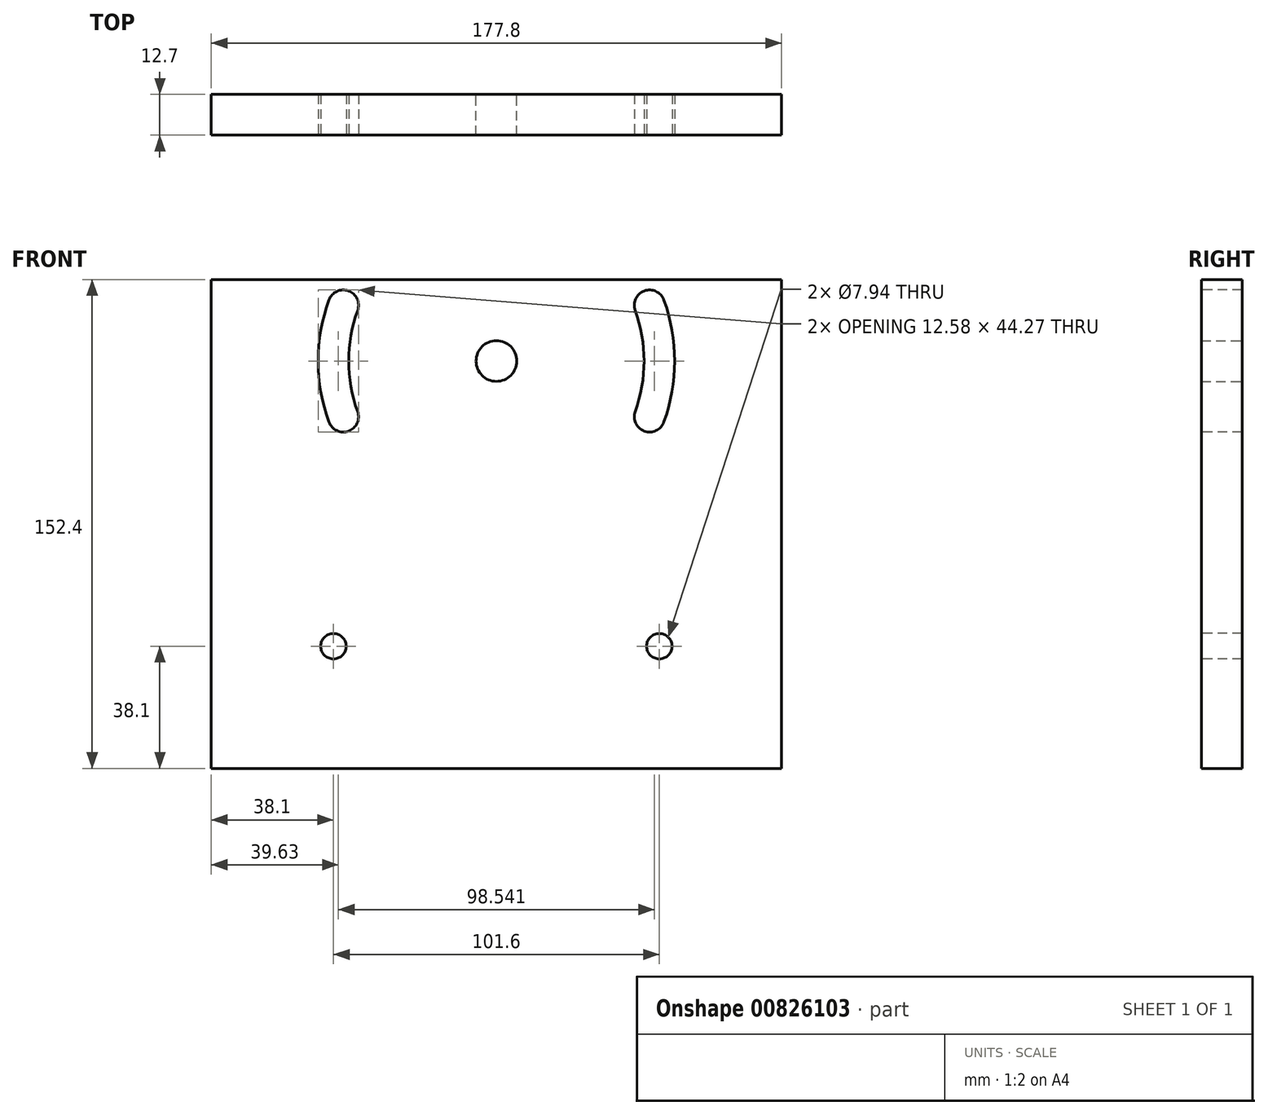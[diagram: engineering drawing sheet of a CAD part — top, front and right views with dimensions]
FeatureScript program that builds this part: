
annotation { "Feature Type Name" : "Feature", "Feature Type Description" : "" }
export const myFeature = defineFeature(function(context is Context, id is Id, definition is map)
    precondition{}
    {
        {
            var Q0;
            Q0=qCreatedBy(makeId("Front.planeOp"),FACE);
            var sketch = newSketch(context, id + "F0", { "sketchPlane" : qUnion([Q0])});
            skCircle(sketch, "E0", {"center": v(0, 0) * mm, "radius": 6.35 * mm});
            skLineSegment(sketch, "E1.bottom", {"start": v(-95.25, -127) * mm, "end": v(88.9, -127) * mm});
            skLineSegment(sketch, "E1.top", {"start": v(-95.25, 25.4) * mm, "end": v(88.9, 25.4) * mm});
            skLineSegment(sketch, "E1.left", {"start": v(-95.25, -127) * mm, "end": v(-95.25, 25.4) * mm});
            skLineSegment(sketch, "E1.right", {"start": v(88.9, -127) * mm, "end": v(88.9, 25.4) * mm});
            skSolve(sketch);
        }
        {
            var Q0;
            Q0=qSketchRegion(id+"F0",true);
            extrude(context, id + "F1", {"entities" : qUnion([Q0]), "depth" : 12.7 * mm, "offsetDistance" : 25.4 * mm});
        }
        {
            var Q0;
            Q0=makeQuery(id+"F1.opExtrude","CAP_FACE",FACE,{"disambiguationData":[OSD([sQuery(id+"F0.wireOp",EDGE,"E0"),sQuery(id+"F0.wireOp",EDGE,"E1.bottom"),sQuery(id+"F0.wireOp",EDGE,"E1.top"),sQuery(id+"F0.wireOp",EDGE,"E1.left"),sQuery(id+"F0.wireOp",EDGE,"E1.right")])],"isStart":false});
            var sketch = newSketch(context, id + "F2", { "sketchPlane" : qUnion([Q0])});
            skCircle(sketch, "E2", {"center": v(0, 0) * mm, "radius": 50.8 * mm, "construction": true});
            skArc(sketch, "E3", {"start": v(52.21, 19) * mm, "mid": v(46.1, 21.85) * mm, "end": v(43.26, 15.75) * mm});
            skArc(sketch, "E4", {"start": v(43.26, -15.75) * mm, "mid": v(46.1, -21.85) * mm, "end": v(52.21, -19) * mm});
            skLineSegment(sketch, "E5", {"start": v(0, 0) * mm, "end": v(47.74, 17.37) * mm, "construction": true});
            skLineSegment(sketch, "E6", {"start": v(0, 0) * mm, "end": v(50.8, 0) * mm, "construction": true});
            skLineSegment(sketch, "E7", {"start": v(0, 0) * mm, "end": v(47.74, -17.37) * mm, "construction": true});
            skArc(sketch, "E8", {"start": v(43.26, -15.75) * mm, "mid": v(46.04, 0) * mm, "end": v(43.26, 15.75) * mm});
            skArc(sketch, "E9", {"start": v(52.21, -19) * mm, "mid": v(55.56, 0) * mm, "end": v(52.21, 19) * mm});
            skSolve(sketch);
        }
        {
            var Q0;
            Q0=qSketchRegion(id+"F2",true);
            extrude(context, id + "F3", {"entities" : qUnion([Q0]), "operationType" : NewBodyOperationType.REMOVE, "endBound" : BoundingType.THROUGH_ALL, "oppositeDirection" : true, "depth" : 25.4 * mm, "offsetDistance" : 25.4 * mm});
        }
        {
            var Q0;
            Q0=makeQuery(id+"F1.opExtrude","SWEPT_BODY",BODY,{"disambiguationData":[OSD([sQuery(id+"F0.wireOp",EDGE,"E0"),sQuery(id+"F0.wireOp",EDGE,"E1.bottom"),sQuery(id+"F0.wireOp",EDGE,"E1.top"),sQuery(id+"F0.wireOp",EDGE,"E1.left"),sQuery(id+"F0.wireOp",EDGE,"E1.right")])]});
            var Q1;
            Q1=qCreatedBy(makeId("Right.planeOp"),FACE);
            mirror(context, id + "F4", {"operationType" : NewBodyOperationType.INTERSECT, "entities" : qUnion([Q0]), "mirrorPlane" : qUnion([Q1])});
        }
        {
            var Q0;
            Q0=makeQuery(id+"F1.opExtrude","CAP_FACE",FACE,{"disambiguationData":[OSD([sQuery(id+"F0.wireOp",EDGE,"E0"),sQuery(id+"F0.wireOp",EDGE,"E1.bottom"),sQuery(id+"F0.wireOp",EDGE,"E1.top"),sQuery(id+"F0.wireOp",EDGE,"E1.left"),sQuery(id+"F0.wireOp",EDGE,"E1.right")])],"isStart":false});
            var sketch = newSketch(context, id + "F5", { "sketchPlane" : qUnion([Q0])});
            skPoint(sketch, "E10", {"position": v(50.8, -88.9) * mm});
            skPoint(sketch, "E11", {"position": v(-50.8, -88.9) * mm});
            skSolve(sketch);
        }
        {
            var Q0;
            Q0=sQuery(id+"F5.wireOp",VERTEX,"E10");
            var Q1;
            Q1=sQuery(id+"F5.wireOp",VERTEX,"E11");
            var Q2;
            Q2=makeQuery(id+"F1.opExtrude","SWEPT_BODY",BODY,{"disambiguationData":[OSD([sQuery(id+"F0.wireOp",EDGE,"E0"),sQuery(id+"F0.wireOp",EDGE,"E1.bottom"),sQuery(id+"F0.wireOp",EDGE,"E1.top"),sQuery(id+"F0.wireOp",EDGE,"E1.left"),sQuery(id+"F0.wireOp",EDGE,"E1.right")])]});
            hole(context, id + "F6", {"style" : HoleStyle.SIMPLE, "endStyle" : HoleEndStyle.THROUGH, "holeDiameter" : 7.94 * mm, "majorDiameter" : 6.35 * mm, "isTappedThrough" : true, "tappedDepth" : 12.7 * mm, "tapClearance" : 3, "locations" : qUnion([Q0, Q1]), "scope" : qUnion([Q2])});
        }
        {
            var Q0;
            Q0=qCreatedBy(makeId("Right.planeOp"),FACE);
            cPlane(context, id + "F7", {"entities" : qUnion([Q0]), "cplaneType" : CPlaneType.OFFSET, "offset" : 24.76 * mm, "width" : 152.4 * mm, "height" : 152.4 * mm});
        }
    });
